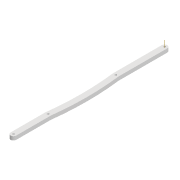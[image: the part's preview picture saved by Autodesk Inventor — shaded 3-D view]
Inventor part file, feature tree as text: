
AUTODESK INVENTOR PART (.ipt)
format: ipt  version: 2022 (Build 260153000, 153)  size: 102,912 bytes
history: native  units: mm
features: extrude x1, other x1, sketch x1
ambient origin geometry x8: Origin, YZ Plane, XZ Plane, XY Plane, X Axis, Y Axis, Z Axis, Center Point
bodies: Solid1 (feature_tree)
feature tree (3):
  extrude  "Extrusion1"  Depth=300.0mm
  other  "Work Axis3"
  sketch  "Sketch1"  dims[d0=2.2mm d1=2.2mm d2=6.0mm d3=163.527mm d4=2.2mm d5=37.565mm d6=4.0mm d7=0.0mm d8=2.2mm d9=110.762mm d10=300.0mm d11=300.0mm]
